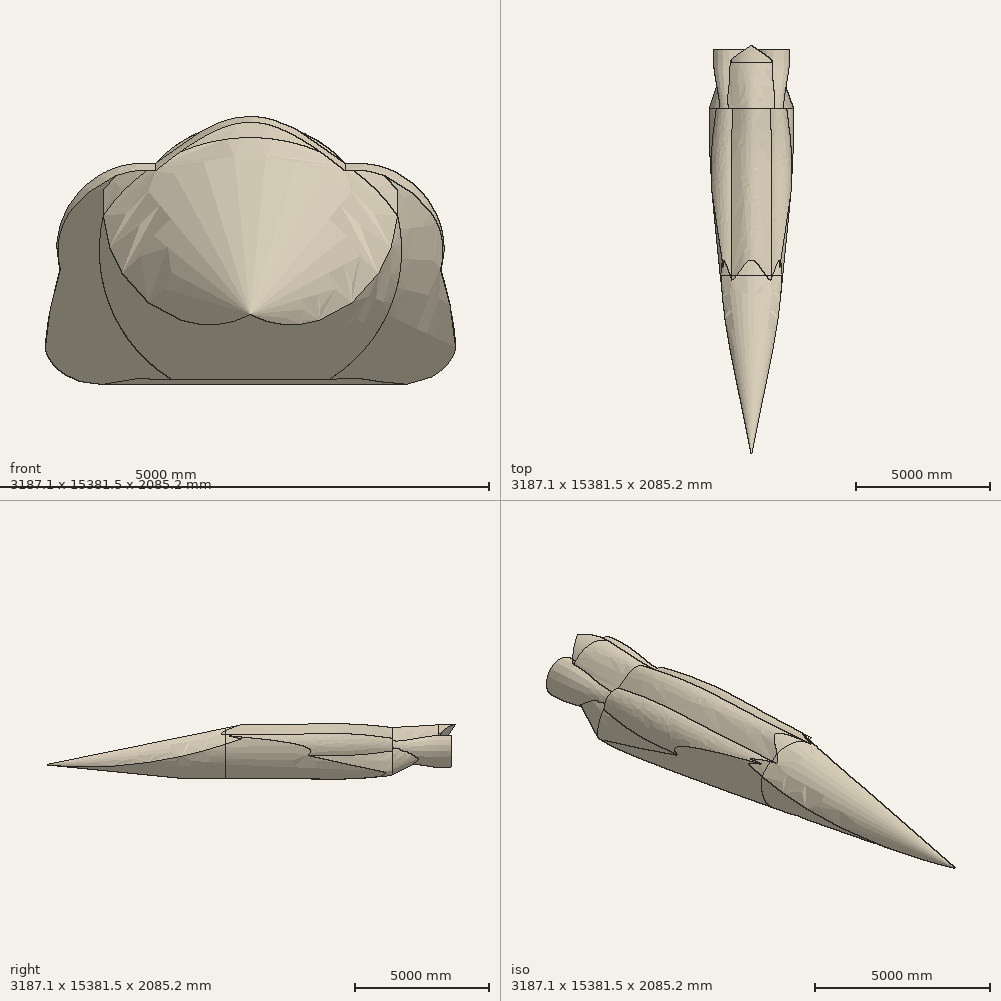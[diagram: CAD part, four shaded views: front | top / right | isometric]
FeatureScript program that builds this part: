
annotation { "Feature Type Name" : "Feature", "Feature Type Description" : "" }
export const myFeature = defineFeature(function(context is Context, id is Id, definition is map)
    precondition{}
    {
        {
            var Q0;
            Q0=qCreatedBy(makeId("Front.planeOp"),FACE);
            cPlane(context, id + "F0", {"entities" : qUnion([Q0]), "cplaneType" : CPlaneType.OFFSET, "offset" : 1750 * mm, "width" : 152.4 * mm, "height" : 152.4 * mm});
        }
        {
            var Q0;
            Q0=qCreatedBy(id+"F0.planeOp",FACE);
            var sketch = newSketch(context, id + "F1", { "sketchPlane" : qUnion([Q0])});
            skLineSegment(sketch, "E0.top", {"start": v(-1394.2, -1000) * mm, "end": v(1394.2, -1000) * mm});
            skPoint(sketch, "E0.middle", {"position": v(0, 0) * mm});
            skFitSpline(sketch, "E1", {"points": [v(-1600, -1000) * mm, v(-848, 530) * mm, v(0, 1000) * mm, v(848, 530) * mm, v(1600, -1000) * mm], "startDerivative": vector(0, 10524.75) * mm, "endDerivative": vector(0, -10524.75) * mm});
            skArc(sketch, "E2", {"start": v(-735.27, 618.52) * mm, "mid": v(-1273.27, 435.52) * mm, "end": v(-1440.68, -107.53) * mm});
            skArc(sketch, "E3.trimOffspring", {"start": v(1440.68, -107.53) * mm, "mid": v(1273.27, 435.52) * mm, "end": v(735.27, 618.52) * mm});
            skFitSpline(sketch, "E4.trimOffspring", {"points": [v(-1600, -1000) * mm, v(-848, 530) * mm, v(0, 1000) * mm, v(848, 530) * mm, v(1600, -1000) * mm], "startDerivative": vector(0, 10524.75) * mm, "endDerivative": vector(0, -10524.75) * mm});
            skFitSpline(sketch, "E5.trimOffspring", {"points": [v(-1600, -1000) * mm, v(-848, 530) * mm, v(0, 1000) * mm, v(848, 530) * mm, v(1600, -1000) * mm], "startDerivative": vector(0, 10524.75) * mm, "endDerivative": vector(0, -10524.75) * mm});
            skArc(sketch, "E6.filletArc", {"start": v(-1593.82, -787.83) * mm, "mid": v(-1539.85, -937.05) * mm, "end": v(-1394.2, -1000) * mm});
            skArc(sketch, "E7.filletArc", {"start": v(1394.2, -1000) * mm, "mid": v(1539.85, -937.05) * mm, "end": v(1593.82, -787.83) * mm});
            skSolve(sketch);
        }
        {
            var Q0;
            Q0=qCreatedBy(makeId("Front.planeOp"),FACE);
            var sketch = newSketch(context, id + "F2", { "sketchPlane" : qUnion([Q0])});
            skLineSegment(sketch, "E8.top", {"start": v(-1394.2, -1000) * mm, "end": v(1394.2, -1000) * mm});
            skPoint(sketch, "E8.middle", {"position": v(0, 0) * mm});
            skFitSpline(sketch, "E9", {"points": [v(-1600, -1000) * mm, v(-848, 530) * mm, v(0, 1000) * mm, v(848, 530) * mm, v(1600, -1000) * mm], "startDerivative": vector(0, 10524.75) * mm, "endDerivative": vector(0, -10524.75) * mm});
            skArc(sketch, "E10", {"start": v(-735.27, 618.52) * mm, "mid": v(-1273.27, 435.52) * mm, "end": v(-1440.68, -107.53) * mm});
            skArc(sketch, "E11.trimOffspring", {"start": v(1440.68, -107.53) * mm, "mid": v(1273.27, 435.52) * mm, "end": v(735.27, 618.52) * mm});
            skFitSpline(sketch, "E12.trimOffspring", {"points": [v(-1600, -1000) * mm, v(-848, 530) * mm, v(0, 1000) * mm, v(848, 530) * mm, v(1600, -1000) * mm], "startDerivative": vector(0, 10524.75) * mm, "endDerivative": vector(0, -10524.75) * mm});
            skFitSpline(sketch, "E13.trimOffspring", {"points": [v(-1600, -1000) * mm, v(-848, 530) * mm, v(0, 1000) * mm, v(848, 530) * mm, v(1600, -1000) * mm], "startDerivative": vector(0, 10524.75) * mm, "endDerivative": vector(0, -10524.75) * mm});
            skArc(sketch, "E14.filletArc", {"start": v(-1593.82, -787.83) * mm, "mid": v(-1539.85, -937.05) * mm, "end": v(-1394.2, -1000) * mm});
            skArc(sketch, "E15.filletArc", {"start": v(1394.2, -1000) * mm, "mid": v(1539.85, -937.05) * mm, "end": v(1593.82, -787.83) * mm});
            skSolve(sketch);
        }
        {
            var Q0;
            Q0=qCreatedBy(makeId("Front.planeOp"),FACE);
            cPlane(context, id + "F3", {"entities" : qUnion([Q0]), "cplaneType" : CPlaneType.OFFSET, "offset" : 3500 * mm, "oppositeDirection" : true, "width" : 150 * mm, "height" : 150 * mm});
        }
        {
            var Q0;
            Q0=qCreatedBy(id+"F3.planeOp",FACE);
            var sketch = newSketch(context, id + "F4", { "sketchPlane" : qUnion([Q0])});
            skLineSegment(sketch, "E16.top", {"start": v(-1394.2, -1000) * mm, "end": v(1394.2, -1000) * mm});
            skPoint(sketch, "E16.middle", {"position": v(0, 0) * mm});
            skFitSpline(sketch, "E17", {"points": [v(-1600, -1000) * mm, v(-848, 530) * mm, v(0, 1000) * mm, v(848, 530) * mm, v(1600, -1000) * mm], "startDerivative": vector(0, 10524.75) * mm, "endDerivative": vector(0, -10524.75) * mm});
            skArc(sketch, "E18", {"start": v(-735.27, 618.52) * mm, "mid": v(-1273.27, 435.52) * mm, "end": v(-1440.68, -107.53) * mm});
            skArc(sketch, "E19.trimOffspring", {"start": v(1440.68, -107.53) * mm, "mid": v(1273.27, 435.52) * mm, "end": v(735.27, 618.52) * mm});
            skFitSpline(sketch, "E20.trimOffspring", {"points": [v(-1600, -1000) * mm, v(-848, 530) * mm, v(0, 1000) * mm, v(848, 530) * mm, v(1600, -1000) * mm], "startDerivative": vector(0, 10524.75) * mm, "endDerivative": vector(0, -10524.75) * mm});
            skFitSpline(sketch, "E21.trimOffspring", {"points": [v(-1600, -1000) * mm, v(-848, 530) * mm, v(0, 1000) * mm, v(848, 530) * mm, v(1600, -1000) * mm], "startDerivative": vector(0, 10524.75) * mm, "endDerivative": vector(0, -10524.75) * mm});
            skArc(sketch, "E22.filletArc", {"start": v(-1593.82, -787.83) * mm, "mid": v(-1539.85, -937.05) * mm, "end": v(-1394.2, -1000) * mm});
            skArc(sketch, "E23.filletArc", {"start": v(1394.2, -1000) * mm, "mid": v(1539.85, -937.05) * mm, "end": v(1593.82, -787.83) * mm});
            skSolve(sketch);
        }
        {
            var Q0;
            Q0=qCreatedBy(makeId("Front.planeOp"),FACE);
            cPlane(context, id + "F5", {"entities" : qUnion([Q0]), "cplaneType" : CPlaneType.OFFSET, "offset" : 4500 * mm, "oppositeDirection" : true, "width" : 150 * mm, "height" : 150 * mm});
        }
        {
            var Q0;
            Q0=qCreatedBy(id+"F5.planeOp",FACE);
            var sketch = newSketch(context, id + "F6", { "sketchPlane" : qUnion([Q0])});
            skLineSegment(sketch, "E24.top", {"start": v(-1413.07, -900) * mm, "end": v(1413.07, -900) * mm});
            skPoint(sketch, "E24.middle", {"position": v(0, 0) * mm});
            skFitSpline(sketch, "E25", {"points": [v(-1600, -900) * mm, v(-784.42, 441.24) * mm, v(0, 900) * mm, v(784.42, 441.24) * mm, v(1600, -900) * mm], "startDerivative": vector(0, 9508.62) * mm, "endDerivative": vector(0, -9508.62) * mm});
            skArc(sketch, "E26", {"start": v(-719.25, 488.69) * mm, "mid": v(-1131.76, 394.84) * mm, "end": v(-1324.66, 18.33) * mm});
            skArc(sketch, "E27.trimOffspring", {"start": v(1324.66, 18.33) * mm, "mid": v(1131.76, 394.84) * mm, "end": v(719.25, 488.69) * mm});
            skFitSpline(sketch, "E28.trimOffspring", {"points": [v(-1600, -900) * mm, v(-784.42, 441.24) * mm, v(0, 900) * mm, v(784.42, 441.24) * mm, v(1600, -900) * mm], "startDerivative": vector(0, 9508.62) * mm, "endDerivative": vector(0, -9508.62) * mm});
            skFitSpline(sketch, "E29.trimOffspring", {"points": [v(-1600, -900) * mm, v(-784.42, 441.24) * mm, v(0, 900) * mm, v(784.42, 441.24) * mm, v(1600, -900) * mm], "startDerivative": vector(0, 9508.62) * mm, "endDerivative": vector(0, -9508.62) * mm});
            skArc(sketch, "E30.filletArc", {"start": v(-1592.48, -705.43) * mm, "mid": v(-1545.4, -842.02) * mm, "end": v(-1413.07, -900) * mm});
            skArc(sketch, "E31.filletArc", {"start": v(1413.07, -900) * mm, "mid": v(1545.4, -842.02) * mm, "end": v(1592.48, -705.43) * mm});
            skLineSegment(sketch, "E32", {"start": v(-719.25, 488.69) * mm, "end": v(-1324.66, 18.33) * mm, "construction": true});
            skLineSegment(sketch, "E33", {"start": v(719.25, 488.69) * mm, "end": v(1324.66, 18.33) * mm, "construction": true});
            skSolve(sketch);
        }
        {
            var Q0;
            Q0=qCreatedBy(makeId("Front.planeOp"),FACE);
            cPlane(context, id + "F7", {"entities" : qUnion([Q0]), "cplaneType" : CPlaneType.OFFSET, "offset" : 6232.05 * mm, "oppositeDirection" : true, "width" : 150 * mm, "height" : 150 * mm});
        }
        {
            var Q0;
            Q0=qCreatedBy(id+"F7.planeOp",FACE);
            var sketch = newSketch(context, id + "F8", { "sketchPlane" : qUnion([Q0])});
            skArc(sketch, "E34", {"start": v(998.61, 52.63) * mm, "mid": v(0, 1000) * mm, "end": v(-998.61, 52.63) * mm});
            skLineSegment(sketch, "E35", {"start": v(0, 0) * mm, "end": v(-948.68, 0) * mm});
            skLineSegment(sketch, "E36", {"start": v(0, 0) * mm, "end": v(948.68, 0) * mm});
            skPoint(sketch, "E37.visualSharp", {"position": v(-1000, 0) * mm});
            skArc(sketch, "E37.filletArc", {"start": v(-998.61, 52.63) * mm, "mid": v(-984.96, 15.59) * mm, "end": v(-948.68, 0) * mm});
            skPoint(sketch, "E38.visualSharp", {"position": v(1000, 0) * mm});
            skArc(sketch, "E38.filletArc", {"start": v(948.68, 0) * mm, "mid": v(984.96, 15.59) * mm, "end": v(998.61, 52.63) * mm});
            skLineSegment(sketch, "E39", {"start": v(0, 1000) * mm, "end": v(0, 675) * mm, "construction": true});
            skPoint(sketch, "E39.endSnap0", {"position": v(0, 1000) * mm});
            skLineSegment(sketch, "E40", {"start": v(0, 675) * mm, "end": v(737.82, 675) * mm, "construction": true});
            skLineSegment(sketch, "E41", {"start": v(0, 675) * mm, "end": v(-737.82, 675) * mm, "construction": true});
            skSolve(sketch);
        }
        {
            var Q0;
            Q0=qSketchRegion(id+"F1",true);
            var Q1;
            Q1=qSketchRegion(id+"F2",true);
            var Q2;
            Q2=qSketchRegion(id+"F4",true);
            var Q3;
            Q3=qSketchRegion(id+"F6",true);
            loft(context, id + "F9", {"sheetProfilesArray" : [{ "sheetProfileEntities" : qUnion([Q0]) }, { "sheetProfileEntities" : qUnion([Q1]) }, { "sheetProfileEntities" : qUnion([Q2]) }, { "sheetProfileEntities" : qUnion([Q3]) }]});
        }
        {
            var Q0;
            Q0=sQuery(id+"F6.wireOp",EDGE,"E32");
            var Q1;
            Q1=sQuery(id+"F8.wireOp",VERTEX,"E41.end");
            cPlane(context, id + "F10", {"entities" : qUnion([Q0, Q1]), "cplaneType" : CPlaneType.LINE_ANGLE, "offset" : 25 * mm, "angle" : 0 * degree, "width" : 150 * mm, "height" : 150 * mm});
        }
        {
            var Q0;
            Q0=qCreatedBy(id+"F10.planeOp",FACE);
            var sketch = newSketch(context, id + "F11", { "sketchPlane" : qUnion([Q0])});
            skLineSegment(sketch, "E42", {"start": v(-589.34, -4526.34) * mm, "end": v(-612.8, -6268.32) * mm});
            skLineSegment(sketch, "E43", {"start": v(-1354.08, -4472.19) * mm, "end": v(-612.8, -6268.32) * mm});
            skSolve(sketch);
        }
        {
            var Q0;
            Q0=sQuery(id+"F6.wireOp",EDGE,"E33");
            var Q1;
            Q1=sQuery(id+"F8.wireOp",VERTEX,"E40.end");
            cPlane(context, id + "F12", {"entities" : qUnion([Q0, Q1]), "cplaneType" : CPlaneType.LINE_ANGLE, "offset" : 25 * mm, "angle" : 0 * degree, "width" : 150 * mm, "height" : 150 * mm});
        }
        {
            var Q0;
            Q0=qCreatedBy(id+"F12.planeOp",FACE);
            var sketch = newSketch(context, id + "F13", { "sketchPlane" : qUnion([Q0])});
            skLineSegment(sketch, "E44", {"start": v(589.34, 4526.34) * mm, "end": v(612.8, 6268.32) * mm});
            skLineSegment(sketch, "E45", {"start": v(1354.08, 4472.19) * mm, "end": v(612.8, 6268.32) * mm});
            skSolve(sketch);
        }
        {
            var Q1;
            Q1=makeQuery(id+"F6.imprint","IMPRINT",FACE,{"disambiguationData":[TD([[makeQuery(id+"F6.imprint","IMPRINT",EDGE,{"derivedFrom":sQuery(id+"F6.wireOp",EDGE,"E24.top")}),1.0]])]});
            var Q2;
            Q2=makeQuery(id+"F8.imprint","IMPRINT",FACE,{"disambiguationData":[TD([[makeQuery(id+"F8.imprint","IMPRINT",EDGE,{"derivedFrom":sQuery(id+"F8.wireOp",EDGE,"E34")}),1.0]])]});
            var Q3;
            Q3=sQuery(id+"F11.wireOp",EDGE,"E42");
            var Q4;
            Q4=sQuery(id+"F13.wireOp",EDGE,"E44");
            loft(context, id + "F14", {"operationType" : NewBodyOperationType.ADD, "addGuides" : true, "sheetProfilesArray" : [{ "sheetProfileEntities" : qUnion([Q1]) }, { "sheetProfileEntities" : qUnion([Q2]) }], "guidesArray" : [{ "guideEntities" : qUnion([Q3]), "guideDerivativeType" : LoftGuideDerivativeType.DEFAULT, "guideDerivativeMagnitude" : 1 }, { "guideEntities" : qUnion([Q4]), "guideDerivativeType" : LoftGuideDerivativeType.DEFAULT, "guideDerivativeMagnitude" : 1 }]});
        }
        {
            var Q0;
            Q0=makeQuery(id+"F14.opLoft","CAP_FACE",FACE,{"disambiguationData":[OSD([makeQuery(id+"F8.imprint","IMPRINT",FACE,{"disambiguationData":[TD([[makeQuery(id+"F8.imprint","IMPRINT",EDGE,{"derivedFrom":sQuery(id+"F8.wireOp",EDGE,"E34")}),1.0]])]})])],"isStart":true});
            extrude(context, id + "F15", {"entities" : qUnion([Q0]), "operationType" : NewBodyOperationType.ADD, "depth" : 649.4 * mm});
        }
        {
            var Q0;
            Q0=qCreatedBy(makeId("Right.planeOp"),FACE);
            var sketch = newSketch(context, id + "F16", { "sketchPlane" : qUnion([Q0])});
            skLineSegment(sketch, "E46", {"start": v(0, 0) * mm, "end": v(4500, 0) * mm});
            skLineSegment(sketch, "E47", {"start": v(4500, 0) * mm, "end": v(6232.05, 0) * mm});
            skLineSegment(sketch, "E48", {"start": v(4500, 0) * mm, "end": v(4500, 1000) * mm});
            skLineSegment(sketch, "E49", {"start": v(4500, 1000) * mm, "end": v(6881.46, 1000) * mm});
            skLineSegment(sketch, "E50", {"start": v(6881.46, 1000) * mm, "end": v(6881.46, -1000) * mm});
            skLineSegment(sketch, "E51", {"start": v(6881.46, 1000) * mm, "end": v(6232.05, 0) * mm});
            skLineSegment(sketch, "E52", {"start": v(6232.05, 0) * mm, "end": v(5582.64, -1000) * mm});
            skLineSegment(sketch, "E53", {"start": v(5582.64, -1000) * mm, "end": v(6881.46, -1000) * mm});
            skSolve(sketch);
        }
        {
            var Q0;
            Q0=makeQuery(id+"F16.imprint","IMPRINT",FACE,{"disambiguationData":[TD([[makeQuery(id+"F16.imprint","IMPRINT",EDGE,{"derivedFrom":sQuery(id+"F16.wireOp",EDGE,"E50")}),-1.0]])]});
            var Q1;
            Q1=sQuery(id+"F16.wireOp",EDGE,"E49");
            revolve(context, id + "F17", {"operationType" : NewBodyOperationType.REMOVE, "entities" : qUnion([Q0]), "axis" : qUnion([Q1]), "revolveType" : RevolveType.SYMMETRIC, "oppositeDirection" : true, "angle" : 182 * degree});
        }
        {
            var Q0;
            Q0=makeQuery(id+"F9.opLoft","CAP_FACE",FACE,{"disambiguationData":[OSD([makeQuery(id+"F1.imprint","IMPRINT",FACE,{"disambiguationData":[TD([[makeQuery(id+"F1.imprint","IMPRINT",EDGE,{"derivedFrom":sQuery(id+"F1.wireOp",EDGE,"E0.top")}),1.0]])]})])],"isStart":true});
            extrude(context, id + "F18", {"entities" : qUnion([Q0]), "depth" : 6750 * mm});
        }
        {
            var Q0;
            Q0=qCreatedBy(makeId("Right.planeOp"),FACE);
            var sketch = newSketch(context, id + "F19", { "sketchPlane" : qUnion([Q0])});
            skLineSegment(sketch, "E54", {"start": v(0, 0) * mm, "end": v(-3500, 0) * mm});
            skLineSegment(sketch, "E55", {"start": v(-3500, 0) * mm, "end": v(-3500, -1000) * mm});
            skLineSegment(sketch, "E56", {"start": v(-3500, -1000) * mm, "end": v(-8500, -1000) * mm});
            skLineSegment(sketch, "E57", {"start": v(-8500, -1000) * mm, "end": v(-8500, -499.31) * mm});
            skLineSegment(sketch, "E58", {"start": v(-1151.4, 0) * mm, "end": v(-1151.4, 1000) * mm});
            skLineSegment(sketch, "E59", {"start": v(-1151.4, 1000) * mm, "end": v(-8500, -499.31) * mm});
            skLineSegment(sketch, "E60", {"start": v(-8500, -499.31) * mm, "end": v(-3500, -1000) * mm});
            skLineSegment(sketch, "E61", {"start": v(-1151.4, 1000) * mm, "end": v(-8500, 1000) * mm});
            skLineSegment(sketch, "E62", {"start": v(-8500, 1000) * mm, "end": v(-8500, -499.31) * mm});
            skLineSegment(sketch, "E63", {"start": v(-8500, -1000) * mm, "end": v(-8500, -1980) * mm});
            skLineSegment(sketch, "E64", {"start": v(-3500, -1000) * mm, "end": v(6286.5, -1980) * mm});
            skLineSegment(sketch, "E65", {"start": v(6286.5, -1980) * mm, "end": v(-8500, -1980) * mm});
            skLineSegment(sketch, "E66", {"start": v(-8500, -499.31) * mm, "end": v(-3500, -499.31) * mm});
            skSolve(sketch);
        }
        {
            var Q0;
            Q0=makeQuery(id+"F19.imprint","IMPRINT",FACE,{"disambiguationData":[TD([[makeQuery(id+"F19.imprint","IMPRINT",EDGE,{"derivedFrom":sQuery(id+"F19.wireOp",EDGE,"E59")}),-1.0]])]});
            var Q1;
            Q1=sQuery(id+"F19.wireOp",EDGE,"E66");
            revolve(context, id + "F20", {"operationType" : NewBodyOperationType.REMOVE, "entities" : qUnion([Q0]), "axis" : qUnion([Q1]), "revolveType" : RevolveType.SYMMETRIC, "oppositeDirection" : true, "angle" : 250 * degree});
        }
        {
            var Q0;
            Q0=makeQuery(id+"F19.imprint","IMPRINT",FACE,{"disambiguationData":[TD([[makeQuery(id+"F19.imprint","IMPRINT",EDGE,{"derivedFrom":sQuery(id+"F19.wireOp",EDGE,"E56")}),-1.0]])]});
            var Q1;
            Q1=makeQuery(id+"F19.imprint","IMPRINT",FACE,{"disambiguationData":[TD([[makeQuery(id+"F19.imprint","IMPRINT",EDGE,{"derivedFrom":sQuery(id+"F19.wireOp",EDGE,"E56")}),1.0]])]});
            var Q2;
            Q2=sQuery(id+"F19.wireOp",EDGE,"E54");
            revolve(context, id + "F21", {"operationType" : NewBodyOperationType.REMOVE, "entities" : qUnion([Q0, Q1]), "axis" : qUnion([Q2]), "revolveType" : RevolveType.SYMMETRIC, "oppositeDirection" : true, "angle" : 240 * degree});
        }
        {
            var Q0;
            Q0=qCreatedBy(makeId("Front.planeOp"),FACE);
            cPlane(context, id + "F22", {"entities" : qUnion([Q0]), "cplaneType" : CPlaneType.OFFSET, "offset" : 3500 * mm, "oppositeDirection" : true, "width" : 150 * mm, "height" : 150 * mm});
        }
        {
            var Q0;
            Q0=qCreatedBy(id+"F22.planeOp",FACE);
            var sketch = newSketch(context, id + "F23", { "sketchPlane" : qUnion([Q0])});
            skCircle(sketch, "E67", {"center": v(-825, 0) * mm, "radius": 600 * mm});
            skCircle(sketch, "E68", {"center": v(825, 0) * mm, "radius": 600 * mm});
            skSolve(sketch);
        }
        {
            var Q0;
            Q0=qCreatedBy(makeId("Front.planeOp"),FACE);
            cPlane(context, id + "F24", {"entities" : qUnion([Q0]), "cplaneType" : CPlaneType.OFFSET, "offset" : 4500 * mm, "oppositeDirection" : true, "width" : 150 * mm, "height" : 150 * mm});
        }
        {
            var Q0;
            Q0=qCreatedBy(id+"F24.planeOp",FACE);
            var sketch = newSketch(context, id + "F25", { "sketchPlane" : qUnion([Q0])});
            skCircle(sketch, "E69", {"center": v(-825, 0) * mm, "radius": 400 * mm});
            skCircle(sketch, "E70", {"center": v(825, 0) * mm, "radius": 400 * mm});
            skSolve(sketch);
        }
        {
            var Q0;
            Q0=qCreatedBy(makeId("Front.planeOp"),FACE);
            cPlane(context, id + "F26", {"entities" : qUnion([Q0]), "cplaneType" : CPlaneType.OFFSET, "offset" : 6232.05 * mm, "oppositeDirection" : true, "width" : 150 * mm, "height" : 150 * mm});
        }
        {
            var Q0;
            Q0=qCreatedBy(id+"F26.planeOp",FACE);
            var sketch = newSketch(context, id + "F27", { "sketchPlane" : qUnion([Q0])});
            skCircle(sketch, "E71", {"center": v(-825, 0) * mm, "radius": 600 * mm});
            skCircle(sketch, "E72", {"center": v(825, 0) * mm, "radius": 600 * mm});
            skSolve(sketch);
        }
        {
            var Q0;
            Q0=qCreatedBy(makeId("Front.planeOp"),FACE);
            cPlane(context, id + "F28", {"entities" : qUnion([Q0]), "cplaneType" : CPlaneType.OFFSET, "offset" : 6732.05 * mm, "oppositeDirection" : true, "width" : 150 * mm, "height" : 150 * mm});
        }
        {
            var Q0;
            Q0=qCreatedBy(id+"F28.planeOp",FACE);
            var sketch = newSketch(context, id + "F29", { "sketchPlane" : qUnion([Q0])});
            skCircle(sketch, "E73", {"center": v(-825, 0) * mm, "radius": 600 * mm});
            skCircle(sketch, "E74", {"center": v(825, 0) * mm, "radius": 600 * mm});
            skSolve(sketch);
        }
        {
            var Q0;
            Q0=makeQuery(id+"F23.imprint","IMPRINT",FACE,{"disambiguationData":[TD([[makeQuery(id+"F23.imprint","IMPRINT",EDGE,{"derivedFrom":sQuery(id+"F23.wireOp",EDGE,"E67")}),1.0]])]});
            var Q1;
            Q1=makeQuery(id+"F25.imprint","IMPRINT",FACE,{"disambiguationData":[TD([[makeQuery(id+"F25.imprint","IMPRINT",EDGE,{"derivedFrom":sQuery(id+"F25.wireOp",EDGE,"E69")}),1.0]])]});
            var Q2;
            Q2=makeQuery(id+"F27.imprint","IMPRINT",FACE,{"disambiguationData":[TD([[makeQuery(id+"F27.imprint","IMPRINT",EDGE,{"derivedFrom":sQuery(id+"F27.wireOp",EDGE,"E71")}),1.0]])]});
            var Q3;
            Q3=makeQuery(id+"F29.imprint","IMPRINT",FACE,{"disambiguationData":[TD([[makeQuery(id+"F29.imprint","IMPRINT",EDGE,{"derivedFrom":sQuery(id+"F29.wireOp",EDGE,"E73")}),1.0]])]});
            loft(context, id + "F30", {"sheetProfilesArray" : [{ "sheetProfileEntities" : qUnion([Q0]) }, { "sheetProfileEntities" : qUnion([Q1]) }, { "sheetProfileEntities" : qUnion([Q2]) }, { "sheetProfileEntities" : qUnion([Q3]) }]});
        }
        {
            var Q0;
            Q0=makeQuery(id+"F23.imprint","IMPRINT",FACE,{"disambiguationData":[TD([[makeQuery(id+"F23.imprint","IMPRINT",EDGE,{"derivedFrom":sQuery(id+"F23.wireOp",EDGE,"E68")}),1.0]])]});
            var Q1;
            Q1=makeQuery(id+"F25.imprint","IMPRINT",FACE,{"disambiguationData":[TD([[makeQuery(id+"F25.imprint","IMPRINT",EDGE,{"derivedFrom":sQuery(id+"F25.wireOp",EDGE,"E70")}),1.0]])]});
            var Q2;
            Q2=makeQuery(id+"F27.imprint","IMPRINT",FACE,{"disambiguationData":[TD([[makeQuery(id+"F27.imprint","IMPRINT",EDGE,{"derivedFrom":sQuery(id+"F27.wireOp",EDGE,"E72")}),1.0]])]});
            var Q3;
            Q3=makeQuery(id+"F29.imprint","IMPRINT",FACE,{"disambiguationData":[TD([[makeQuery(id+"F29.imprint","IMPRINT",EDGE,{"derivedFrom":sQuery(id+"F29.wireOp",EDGE,"E74")}),1.0]])]});
            loft(context, id + "F31", {"sheetProfilesArray" : [{ "sheetProfileEntities" : qUnion([Q0]) }, { "sheetProfileEntities" : qUnion([Q1]) }, { "sheetProfileEntities" : qUnion([Q2]) }, { "sheetProfileEntities" : qUnion([Q3]) }]});
        }
    });
